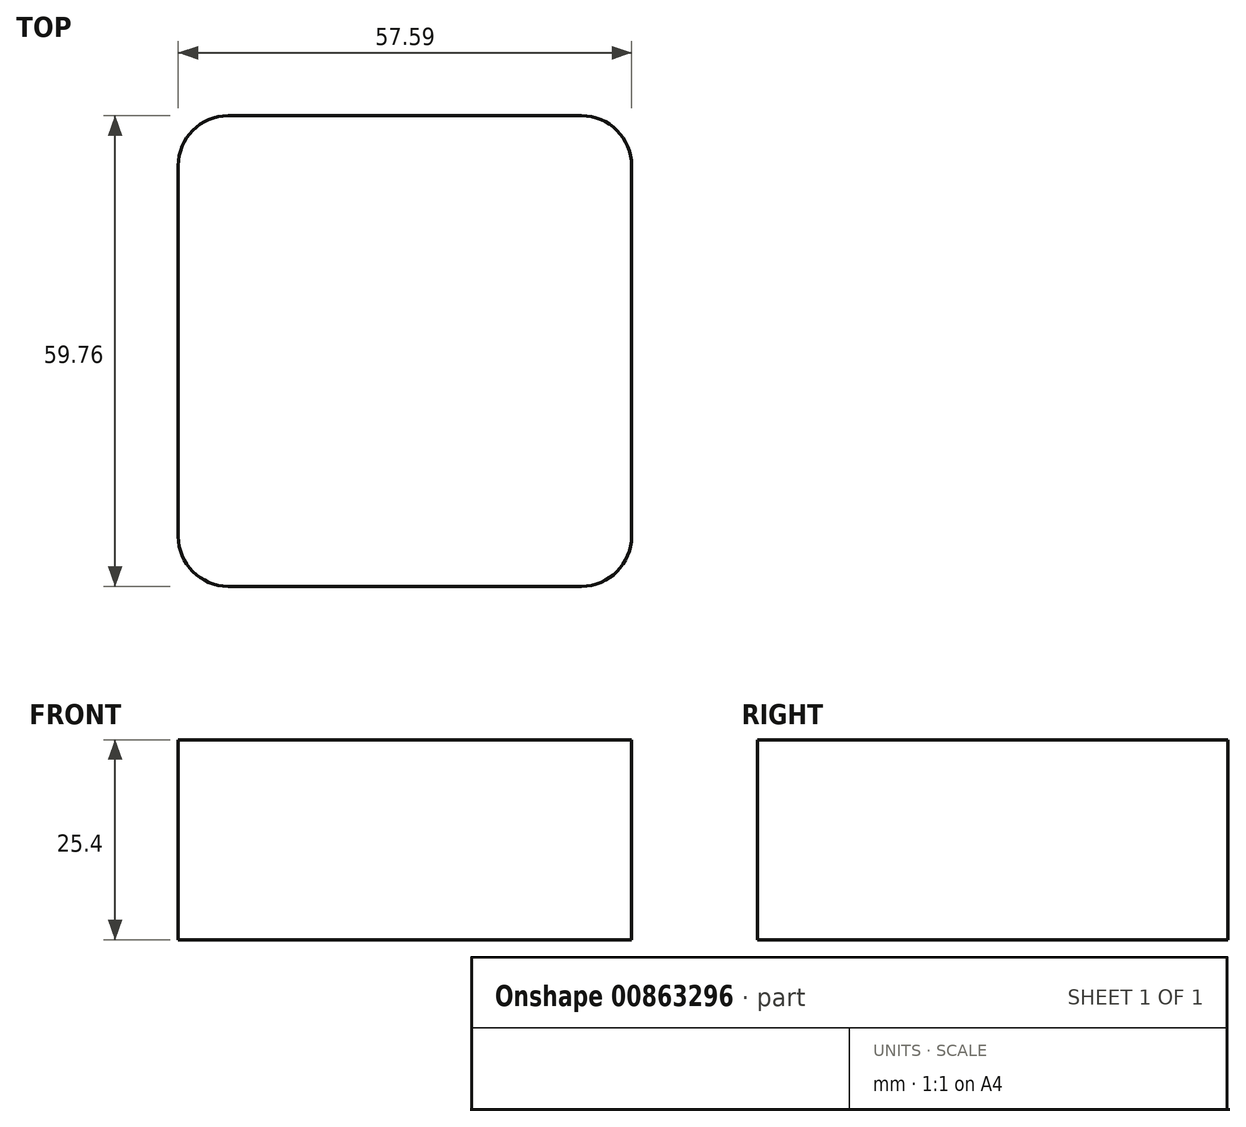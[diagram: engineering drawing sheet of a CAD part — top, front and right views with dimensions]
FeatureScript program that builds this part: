
annotation { "Feature Type Name" : "Feature", "Feature Type Description" : "" }
export const myFeature = defineFeature(function(context is Context, id is Id, definition is map)
    precondition{}
    {
        {
            var Q0;
            Q0=qCreatedBy(makeId("Top.planeOp"),FACE);
            var sketch = newSketch(context, id + "F0", { "sketchPlane" : qUnion([Q0])});
            skLineSegment(sketch, "E0.bottom", {"start": v(-19.63, -31.18) * mm, "end": v(25.26, -31.18) * mm});
            skLineSegment(sketch, "E0.top", {"start": v(-19.63, 28.58) * mm, "end": v(25.26, 28.58) * mm});
            skLineSegment(sketch, "E0.left", {"start": v(-25.98, -24.83) * mm, "end": v(-25.98, 22.23) * mm});
            skLineSegment(sketch, "E0.right", {"start": v(31.61, -24.83) * mm, "end": v(31.61, 22.23) * mm});
            skPoint(sketch, "E1.visualSharp", {"position": v(31.61, 28.58) * mm});
            skArc(sketch, "E1.filletArc", {"start": v(31.61, 22.23) * mm, "mid": v(29.75, 26.72) * mm, "end": v(25.26, 28.58) * mm});
            skPoint(sketch, "E2.visualSharp", {"position": v(-25.98, -31.18) * mm});
            skArc(sketch, "E2.filletArc", {"start": v(-25.98, -24.83) * mm, "mid": v(-24.12, -29.32) * mm, "end": v(-19.63, -31.18) * mm});
            skPoint(sketch, "E3.visualSharp", {"position": v(31.61, -31.18) * mm});
            skArc(sketch, "E3.filletArc", {"start": v(25.26, -31.18) * mm, "mid": v(29.75, -29.32) * mm, "end": v(31.61, -24.83) * mm});
            skPoint(sketch, "E4.visualSharp", {"position": v(-25.98, 28.58) * mm});
            skArc(sketch, "E4.filletArc", {"start": v(-19.63, 28.58) * mm, "mid": v(-24.12, 26.72) * mm, "end": v(-25.98, 22.23) * mm});
            skSolve(sketch);
        }
        {
            var Q0;
            Q0 = qSketchRegion(id + "F0", true);
            extrude(context, id + "F1", {"entities" : qUnion([Q0]), "oppositeDirection" : true, "depth" : 25.4 * mm, "offsetDistance" : 25.4 * mm});
        }
    });
